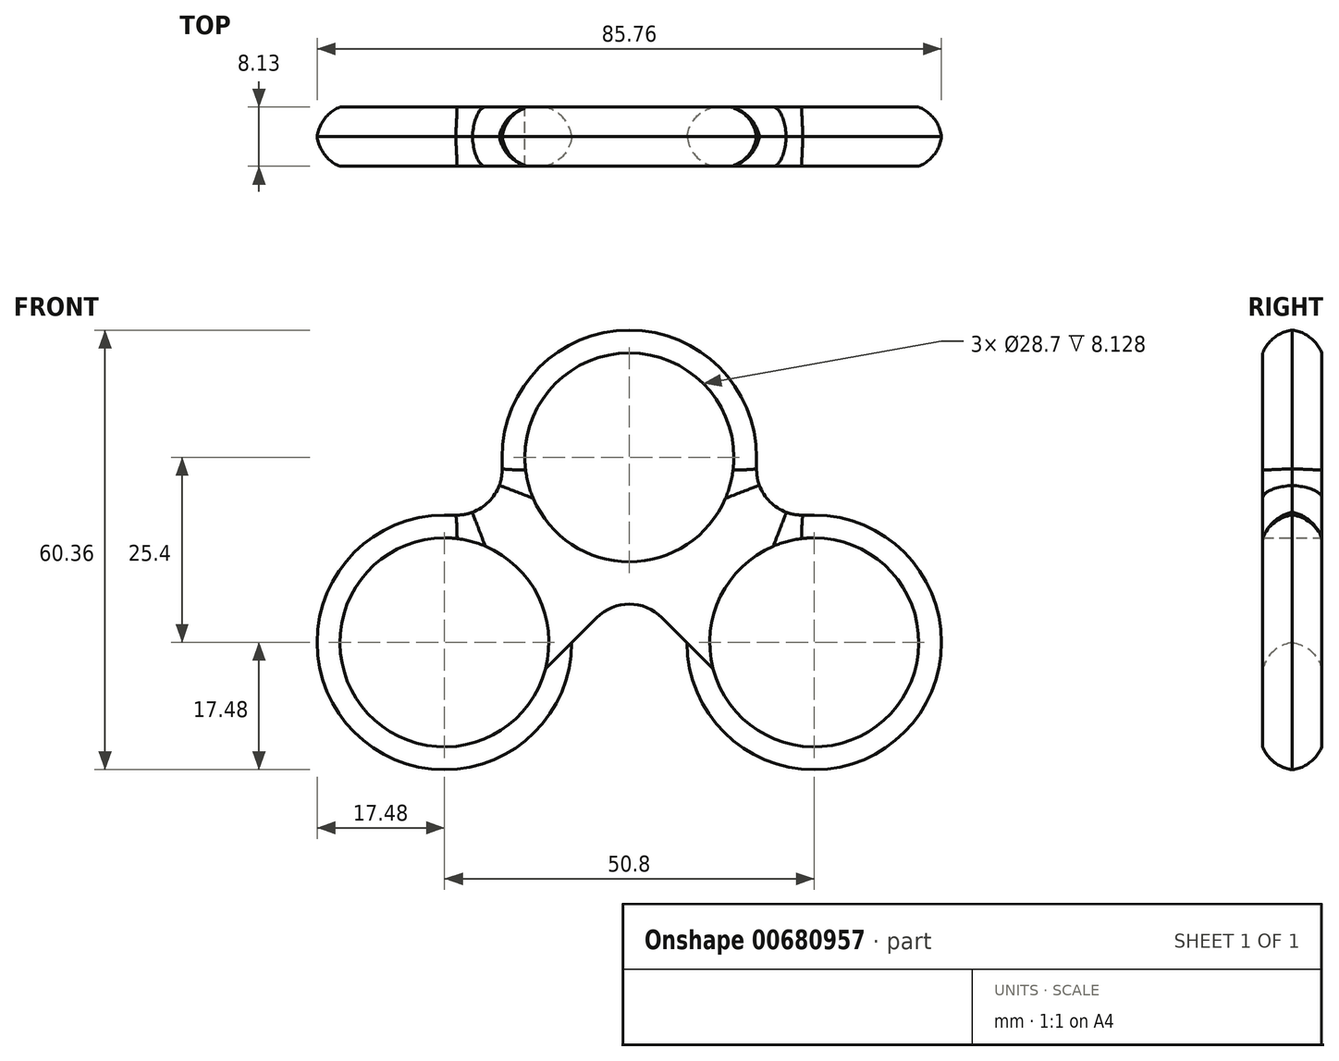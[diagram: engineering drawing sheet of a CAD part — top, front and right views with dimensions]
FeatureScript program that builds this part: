
annotation { "Feature Type Name" : "Feature", "Feature Type Description" : "" }
export const myFeature = defineFeature(function(context is Context, id is Id, definition is map)
    precondition{}
    {
        {
            var Q0;
            Q0=qCreatedBy(makeId("Front.planeOp"),FACE);
            var sketch = newSketch(context, id + "F0", { "sketchPlane" : qUnion([Q0])});
            skCircle(sketch, "E0", {"center": v(0, 0) * mm, "radius": 14.35 * mm});
            skCircle(sketch, "E1", {"center": v(-25.4, -25.4) * mm, "radius": 14.35 * mm});
            skCircle(sketch, "E2", {"center": v(25.4, -25.4) * mm, "radius": 14.35 * mm});
            skArc(sketch, "E3", {"start": v(-25.4, -7.87) * mm, "mid": v(-42.93, -25.4) * mm, "end": v(-25.4, -42.93) * mm});
            skArc(sketch, "E4.MirrorCS", {"start": v(25.4, -7.87) * mm, "mid": v(42.93, -25.4) * mm, "end": v(25.4, -42.93) * mm});
            skArc(sketch, "E5", {"start": v(-25.4, -42.93) * mm, "mid": v(-13, -37.8) * mm, "end": v(-7.87, -25.4) * mm});
            skArc(sketch, "E6.MirrorCS", {"start": v(25.4, -42.93) * mm, "mid": v(13, -37.8) * mm, "end": v(7.87, -25.4) * mm});
            skLineSegment(sketch, "E7", {"start": v(-7.87, -25.4) * mm, "end": v(-4.5, -22.02) * mm});
            skLineSegment(sketch, "E8", {"start": v(4.5, -22.02) * mm, "end": v(7.87, -25.4) * mm});
            skPoint(sketch, "E9.visualSharp", {"position": v(0, -17.53) * mm});
            skArc(sketch, "E9.filletArc", {"start": v(4.5, -22.02) * mm, "mid": v(0, -20.16) * mm, "end": v(-4.5, -22.02) * mm});
            skArc(sketch, "E10", {"start": v(0, 17.53) * mm, "mid": v(-12.4, 12.4) * mm, "end": v(-17.53, 0) * mm});
            skArc(sketch, "E11.MirrorCS", {"start": v(0, 17.53) * mm, "mid": v(12.4, 12.4) * mm, "end": v(17.53, 0) * mm});
            skLineSegment(sketch, "E12", {"start": v(-25.4, -7.87) * mm, "end": v(-23.88, -7.87) * mm});
            skLineSegment(sketch, "E13", {"start": v(-17.53, -1.52) * mm, "end": v(-17.53, 0) * mm});
            skLineSegment(sketch, "E14", {"start": v(25.4, -7.87) * mm, "end": v(23.88, -7.87) * mm});
            skLineSegment(sketch, "E15", {"start": v(17.53, 0) * mm, "end": v(17.53, -1.52) * mm});
            skPoint(sketch, "E16.visualSharp", {"position": v(-17.53, -7.87) * mm});
            skArc(sketch, "E16.filletArc", {"start": v(-23.88, -7.87) * mm, "mid": v(-19.39, -6.01) * mm, "end": v(-17.53, -1.52) * mm});
            skPoint(sketch, "E17.visualSharp", {"position": v(17.53, -7.87) * mm});
            skArc(sketch, "E17.filletArc", {"start": v(17.53, -1.52) * mm, "mid": v(19.39, -6.01) * mm, "end": v(23.88, -7.87) * mm});
            skSolve(sketch);
        }
        {
            var Q0;
            Q0 = qSketchRegion(id + "F0", true);
            extrude(context, id + "F1", {"entities" : qUnion([Q0]), "depth" : 8.13 * mm, "offsetDistance" : 25.4 * mm});
        }
        {
            var Q0;
            Q0=makeQuery(id+"F1.opExtrude","CAP_EDGE",EDGE,{"disambiguationData":[OSD([sQuery(id+"F0.wireOp",EDGE,"E3"),sQuery(id+"F0.wireOp",EDGE,"E5")])],"isStart":true});
            var Q1;
            Q1=makeQuery(id+"F1.opExtrude","CAP_EDGE",EDGE,{"disambiguationData":[OSD([sQuery(id+"F0.wireOp",EDGE,"E3"),sQuery(id+"F0.wireOp",EDGE,"E5")])],"isStart":false});
            fillet(context, id + "F2", {"entities" : qUnion([Q0, Q1]), "radius" : 5.08 * mm, "tangentPropagation" : true, "allowEdgeOverflow" : false});
        }
    });
